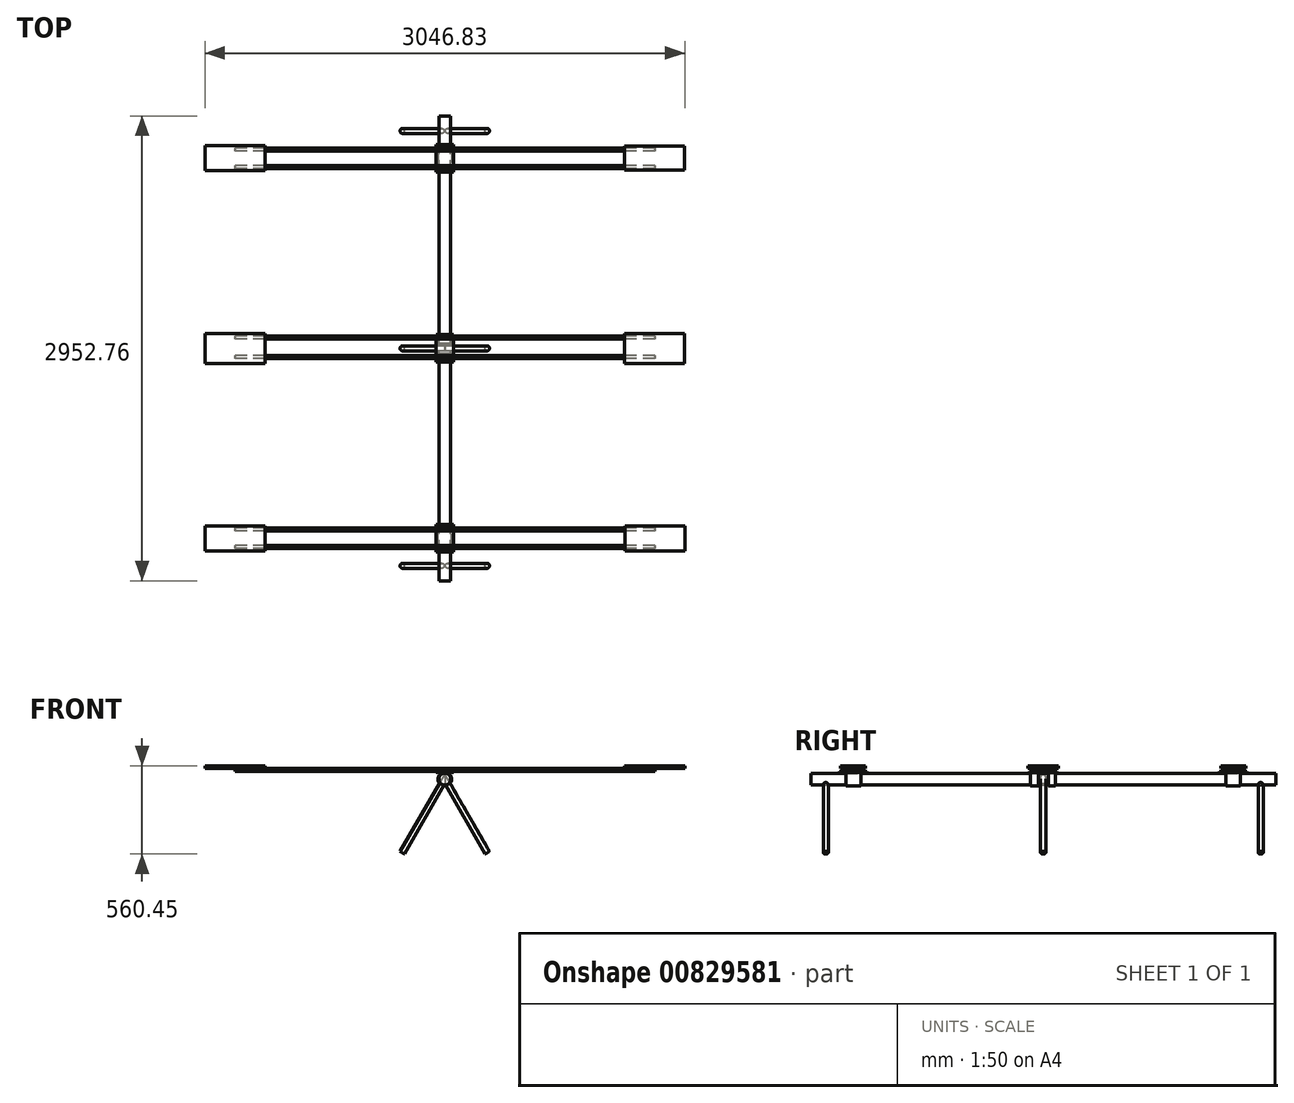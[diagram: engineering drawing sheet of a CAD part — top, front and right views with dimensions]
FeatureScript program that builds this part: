
annotation { "Feature Type Name" : "Feature", "Feature Type Description" : "" }
export const myFeature = defineFeature(function(context is Context, id is Id, definition is map)
    precondition{}
    {
        {
            var Q0;
            Q0=qCreatedBy(makeId("Right.planeOp"),FACE);
            var sketch = newSketch(context, id + "F0", { "sketchPlane" : qUnion([Q0])});
            skLineSegment(sketch, "E0", {"start": v(0, 0) * mm, "end": v(-1104.9, 0) * mm});
            skLineSegment(sketch, "E1", {"start": v(0, 0) * mm, "end": v(1104.9, 0) * mm});
            skPoint(sketch, "E2", {"position": v(-1104.9, 0) * mm});
            skPoint(sketch, "E3", {"position": v(1104.9, 0) * mm});
            skPoint(sketch, "E4", {"position": v(0, 0) * mm});
            skSolve(sketch);
        }
        {
            var Q0;
            Q0=sQuery(id+"F0.wireOp",VERTEX,"E2");
            var Q1;
            Q1=sQuery(id+"F0.wireOp",EDGE,"E0");
            cPlane(context, id + "F1", {"entities" : qUnion([Q0, Q1]), "cplaneType" : CPlaneType.LINE_POINT, "offset" : 25.4 * mm, "width" : 152.4 * mm, "height" : 152.4 * mm});
        }
        {
            var Q0;
            Q0=qCreatedBy(id+"F1.planeOp",FACE);
            var sketch = newSketch(context, id + "F2", { "sketchPlane" : qUnion([Q0])});
            skLineSegment(sketch, "E5", {"start": v(0, 0) * mm, "end": v(215.9, -373.95) * mm});
            skLineSegment(sketch, "E6", {"start": v(0, 0) * mm, "end": v(-215.9, -373.95) * mm});
            skSolve(sketch);
        }
        {
            var Q0;
            Q0=sQuery(id+"F0.wireOp",VERTEX,"E3");
            var Q1;
            Q1=sQuery(id+"F0.wireOp",EDGE,"E1");
            cPlane(context, id + "F3", {"entities" : qUnion([Q0, Q1]), "cplaneType" : CPlaneType.LINE_POINT, "offset" : 25.4 * mm, "width" : 152.4 * mm, "height" : 152.4 * mm});
        }
        {
            var Q0;
            Q0=qCreatedBy(id+"F3.planeOp",FACE);
            var sketch = newSketch(context, id + "F4", { "sketchPlane" : qUnion([Q0])});
            skLineSegment(sketch, "E7", {"start": v(0, 0) * mm, "end": v(215.9, -373.95) * mm});
            skLineSegment(sketch, "E8", {"start": v(0, 0) * mm, "end": v(-215.9, -373.95) * mm});
            skSolve(sketch);
        }
        {
            var Q0;
            Q0=qCreatedBy(makeId("Front.planeOp"),FACE);
            var sketch = newSketch(context, id + "F5", { "sketchPlane" : qUnion([Q0])});
            skLineSegment(sketch, "E9", {"start": v(0, 0) * mm, "end": v(215.9, -373.95) * mm});
            skLineSegment(sketch, "E10", {"start": v(0, 0) * mm, "end": v(-215.9, -373.95) * mm});
            skSolve(sketch);
        }
        {
            var Q0;
            Q0=qCreatedBy(id+"F1.planeOp",FACE);
            var sketch = newSketch(context, id + "F6", { "sketchPlane" : qUnion([Q0])});
            skCircle(sketch, "E11", {"center": v(0, 0) * mm, "radius": 30.16 * mm});
            skSolve(sketch);
        }
        {
            var Q0;
            Q0=makeQuery(id+"F6.imprint","IMPRINT",FACE,{"disambiguationData":[TD([[makeQuery(id+"F6.imprint","IMPRINT",EDGE,{"derivedFrom":sQuery(id+"F6.wireOp",EDGE,"E11")}),1.0]])]});
            var Q1;
            Q1=sQuery(id+"F6.wireOp",EDGE,"E11");
            var Q2;
            Q2=sQuery(id+"F0.wireOp",EDGE,"E0");
            var Q3;
            Q3=sQuery(id+"F0.wireOp",EDGE,"E1");
            sweep(context, id + "F7", {"profiles" : qUnion([Q0]), "surfaceProfiles" : qUnion([Q1]), "path" : qUnion([Q2, Q3])});
        }
        {
            var Q0;
            Q0=makeQuery(id+"F6.imprint","IMPRINT",FACE,{"disambiguationData":[TD([[makeQuery(id+"F6.imprint","IMPRINT",EDGE,{"derivedFrom":sQuery(id+"F6.wireOp",EDGE,"E11")}),1.0]])]});
            extrude(context, id + "F8", {"entities" : qUnion([Q0]), "operationType" : NewBodyOperationType.ADD, "depth" : 76.2 * mm, "offsetDistance" : 25.4 * mm});
        }
        {
            var Q0;
            Q0=sQuery(id+"F2.wireOp",EDGE,"E5");
            var Q1;
            Q1=sQuery(id+"F2.wireOp",VERTEX,"E5.end");
            cPlane(context, id + "F9", {"entities" : qUnion([Q0, Q1]), "cplaneType" : CPlaneType.LINE_POINT, "offset" : 25.4 * mm, "width" : 152.4 * mm, "height" : 152.4 * mm});
        }
        {
            var Q0;
            Q0=qCreatedBy(id+"F9.planeOp",FACE);
            var sketch = newSketch(context, id + "F10", { "sketchPlane" : qUnion([Q0])});
            skPoint(sketch, "E12", {"position": v(0, 1104.9) * mm});
            skCircle(sketch, "E13", {"center": v(0, 1104.9) * mm, "radius": 12.7 * mm});
            skSolve(sketch);
        }
        {
            var Q0;
            Q0=makeQuery(id+"F10.imprint","IMPRINT",FACE,{"disambiguationData":[TD([[makeQuery(id+"F10.imprint","IMPRINT",EDGE,{"derivedFrom":sQuery(id+"F10.wireOp",EDGE,"E13")}),1.0]])]});
            var Q1;
            Q1=sQuery(id+"F2.wireOp",EDGE,"E5");
            var Q2;
            Q2=sQuery(id+"F2.wireOp",EDGE,"E6");
            var Q3;
            Q3 = qConstructionFilter(qBodyType(qCreatedBy(id + "FF3xF3cxVK8Cgxf_1" ,EDGE), BodyType.WIRE), ConstructionObject.NO);
            sweep(context, id + "F11", {"operationType" : NewBodyOperationType.ADD, "profiles" : qUnion([Q0]), "path" : qUnion([Q1, Q2, Q3])});
        }
        {
            var Q0;
            Q0=qCreatedBy(id+"F9.planeOp",FACE);
            var sketch = newSketch(context, id + "F12", { "sketchPlane" : qUnion([Q0])});
            skCircle(sketch, "E14", {"center": v(0, 0) * mm, "radius": 12.7 * mm});
            skSolve(sketch);
        }
        {
            var Q0;
            Q0=makeQuery(id+"F12.imprint","IMPRINT",FACE,{"disambiguationData":[TD([[makeQuery(id+"F12.imprint","IMPRINT",EDGE,{"derivedFrom":sQuery(id+"F12.wireOp",EDGE,"E14")}),1.0]])]});
            var Q1;
            Q1=sQuery(id+"F12.wireOp",EDGE,"E14");
            var Q2;
            Q2=sQuery(id+"F5.wireOp",EDGE,"E9");
            var Q3;
            Q3=sQuery(id+"F5.wireOp",EDGE,"E10");
            sweep(context, id + "F13", {"profiles" : qUnion([Q0]), "surfaceProfiles" : qUnion([Q1]), "path" : qUnion([Q2, Q3])});
        }
        {
            var Q0;
            Q0=qCreatedBy(id+"F9.planeOp",FACE);
            var sketch = newSketch(context, id + "F14", { "sketchPlane" : qUnion([Q0])});
            skCircle(sketch, "E15", {"center": v(0, -1104.9) * mm, "radius": 12.7 * mm});
            skSolve(sketch);
        }
        {
            var Q0;
            Q0=makeQuery(id+"F14.imprint","IMPRINT",FACE,{"disambiguationData":[TD([[makeQuery(id+"F14.imprint","IMPRINT",EDGE,{"derivedFrom":sQuery(id+"F14.wireOp",EDGE,"E15")}),1.0]])]});
            var Q1;
            Q1=sQuery(id+"F4.wireOp",EDGE,"E8");
            var Q2;
            Q2=sQuery(id+"F4.wireOp",EDGE,"E7");
            sweep(context, id + "F15", {"operationType" : NewBodyOperationType.ADD, "profiles" : qUnion([Q0]), "path" : qUnion([Q1, Q2])});
        }
        {
            var Q0;
            Q0=sQuery(id+"F4.wireOp",VERTEX,"E7.start");
            var Q1;
            {var subQ0=sQuery(id+"F6.wireOp",EDGE,"E11");Q1=makeQuery(id+"F8.boolean.opBoolean","MERGE",FACE,{"derivedFrom":[makeQuery(id+"F7.opSweep","SWEPT_FACE",FACE,{"disambiguationData":[OSD([sQuery(id+"F0.wireOp",EDGE,"E0"),subQ0])]}),makeQuery(id+"F8.opExtrude","SWEPT_FACE",FACE,{"disambiguationData":[OSD([subQ0])]})]});}
            cPlane(context, id + "F16", {"entities" : qUnion([Q0, Q1]), "cplaneType" : CPlaneType.LINE_POINT, "offset" : 25.4 * mm, "width" : 152.4 * mm, "height" : 152.4 * mm});
        }
        {
            var Q0;
            Q0=qCreatedBy(id+"F16.planeOp",FACE);
            var sketch = newSketch(context, id + "F17", { "sketchPlane" : qUnion([Q0])});
            skPoint(sketch, "E16", {"position": v(0, 0) * mm});
            skCircle(sketch, "E17", {"center": v(0, 0) * mm, "radius": 30.16 * mm});
            skSolve(sketch);
        }
        {
            var Q0;
            Q0 = qSketchRegion(id + "F17", true);
            extrude(context, id + "F18", {"entities" : qUnion([Q0]), "operationType" : NewBodyOperationType.ADD, "depth" : 76.2 * mm, "offsetDistance" : 25.4 * mm});
        }
        {
            var Q0;
            Q0=qCreatedBy(makeId("Right.planeOp"),FACE);
            var sketch = newSketch(context, id + "F19", { "sketchPlane" : qUnion([Q0])});
            skLineSegment(sketch, "E18", {"start": v(0, 0) * mm, "end": v(-965.2, 0) * mm});
            skLineSegment(sketch, "E19", {"start": v(0, 0) * mm, "end": v(965.2, 0) * mm});
            skSolve(sketch);
        }
        {
            var Q0;
            Q0=sQuery(id+"F19.wireOp",VERTEX,"E18.end");
            var Q1;
            Q1=sQuery(id+"F19.wireOp",EDGE,"E18");
            cPlane(context, id + "F20", {"entities" : qUnion([Q0, Q1]), "cplaneType" : CPlaneType.LINE_POINT, "offset" : 25.4 * mm, "width" : 152.4 * mm, "height" : 152.4 * mm});
        }
        {
            var Q0;
            Q0=qCreatedBy(id+"F20.planeOp",FACE);
            var sketch = newSketch(context, id + "F21", { "sketchPlane" : qUnion([Q0])});
            skPoint(sketch, "E20", {"position": v(0, 0) * mm});
            skCircle(sketch, "E21", {"center": v(0, 0) * mm, "radius": 34.93 * mm});
            skSolve(sketch);
        }
        {
            var Q0;
            Q0=makeQuery(id+"F21.imprint","IMPRINT",FACE,{"disambiguationData":[TD([[makeQuery(id+"F21.imprint","IMPRINT",EDGE,{"derivedFrom":sQuery(id+"F21.wireOp",EDGE,"E21")}),1.0]])]});
            extrude(context, id + "F22", {"entities" : qUnion([Q0]), "depth" : 38.1 * mm, "offsetDistance" : 25.4 * mm, "hasSecondDirection" : true, "secondDirectionOppositeDirection" : true, "secondDirectionDepth" : 38.1 * mm});
        }
        {
            var Q0;
            Q0=sQuery(id+"F19.wireOp",VERTEX,"E19.end");
            var Q1;
            Q1=sQuery(id+"F19.wireOp",EDGE,"E19");
            cPlane(context, id + "F23", {"entities" : qUnion([Q0, Q1]), "cplaneType" : CPlaneType.LINE_POINT, "offset" : 25.4 * mm, "width" : 152.4 * mm, "height" : 152.4 * mm});
        }
        {
            var Q0;
            Q0=qCreatedBy(id+"F23.planeOp",FACE);
            var sketch = newSketch(context, id + "F24", { "sketchPlane" : qUnion([Q0])});
            skPoint(sketch, "E22", {"position": v(0, 0) * mm});
            skCircle(sketch, "E23", {"center": v(0, 0) * mm, "radius": 34.93 * mm});
            skSolve(sketch);
        }
        {
            var Q0;
            Q0 = qSketchRegion(id + "F24", true);
            extrude(context, id + "F25", {"entities" : qUnion([Q0]), "depth" : 38.1 * mm, "offsetDistance" : 25.4 * mm, "hasSecondDirection" : true, "secondDirectionOppositeDirection" : true, "secondDirectionDepth" : 38.1 * mm});
        }
        {
            var Q0;
            Q0=qCreatedBy(makeId("Right.planeOp"),FACE);
            var sketch = newSketch(context, id + "F26", { "sketchPlane" : qUnion([Q0])});
            skLineSegment(sketch, "E24", {"start": v(0, 0) * mm, "end": v(-25.4, 0) * mm});
            skLineSegment(sketch, "E25", {"start": v(0, 0) * mm, "end": v(25.4, 0) * mm});
            skSolve(sketch);
        }
        {
            var Q0;
            Q0=sQuery(id+"F26.wireOp",VERTEX,"E24.end");
            var Q1;
            Q1=sQuery(id+"F26.wireOp",EDGE,"E24");
            cPlane(context, id + "F27", {"entities" : qUnion([Q0, Q1]), "cplaneType" : CPlaneType.LINE_POINT, "offset" : 25.4 * mm, "width" : 152.4 * mm, "height" : 152.4 * mm});
        }
        {
            var Q0;
            Q0=qCreatedBy(id+"F27.planeOp",FACE);
            var sketch = newSketch(context, id + "F28", { "sketchPlane" : qUnion([Q0])});
            skPoint(sketch, "E26", {"position": v(0, 0) * mm});
            skCircle(sketch, "E27", {"center": v(0, 0) * mm, "radius": 34.93 * mm});
            skSolve(sketch);
        }
        {
            var Q0;
            Q0 = qSketchRegion(id + "F28", true);
            extrude(context, id + "F29", {"entities" : qUnion([Q0]), "depth" : 38.1 * mm, "offsetDistance" : 25.4 * mm});
        }
        {
            var Q0;
            Q0=sQuery(id+"F26.wireOp",VERTEX,"E25.end");
            var Q1;
            Q1=sQuery(id+"F26.wireOp",EDGE,"E25");
            cPlane(context, id + "F30", {"entities" : qUnion([Q0, Q1]), "cplaneType" : CPlaneType.LINE_POINT, "offset" : 25.4 * mm, "width" : 152.4 * mm, "height" : 152.4 * mm});
        }
        {
            var Q0;
            Q0=qCreatedBy(id+"F30.planeOp",FACE);
            var sketch = newSketch(context, id + "F31", { "sketchPlane" : qUnion([Q0])});
            skCircle(sketch, "E28", {"center": v(0, 0) * mm, "radius": 34.93 * mm});
            skSolve(sketch);
        }
        {
            var Q0;
            Q0 = qSketchRegion(id + "F31", true);
            extrude(context, id + "F32", {"entities" : qUnion([Q0]), "depth" : 38.1 * mm, "offsetDistance" : 25.4 * mm});
        }
        {
            var Q0;
            Q0=qCreatedBy(id+"F27.planeOp",FACE);
            var sketch = newSketch(context, id + "F33", { "sketchPlane" : qUnion([Q0])});
            skLineSegment(sketch, "E29", {"start": v(0, 0) * mm, "end": v(0, 34.93) * mm});
            skSolve(sketch);
        }
        {
            var Q0;
            Q0=sQuery(id+"F33.wireOp",EDGE,"E29");
            var Q1;
            Q1=sQuery(id+"F33.wireOp",VERTEX,"E29.end");
            cPlane(context, id + "F34", {"entities" : qUnion([Q0, Q1]), "cplaneType" : CPlaneType.LINE_POINT, "offset" : 25.4 * mm, "width" : 152.4 * mm, "height" : 152.4 * mm});
        }
        {
            var Q0;
            Q0=qCreatedBy(id+"F34.planeOp",FACE);
            var sketch = newSketch(context, id + "F35", { "sketchPlane" : qUnion([Q0])});
            skLineSegment(sketch, "E30.bottom", {"start": v(44.45, -69.85) * mm, "end": v(-44.45, -69.85) * mm});
            skLineSegment(sketch, "E30.top", {"start": v(44.45, 69.85) * mm, "end": v(-44.45, 69.85) * mm});
            skLineSegment(sketch, "E30.left", {"start": v(44.45, -69.85) * mm, "end": v(44.45, 69.85) * mm});
            skLineSegment(sketch, "E30.right", {"start": v(-44.45, -69.85) * mm, "end": v(-44.45, 69.85) * mm});
            skPoint(sketch, "E30.middle", {"position": v(0, 0) * mm});
            skSolve(sketch);
        }
        {
            var Q0;
            Q0=qCreatedBy(id+"F34.planeOp",FACE);
            var sketch = newSketch(context, id + "F36", { "sketchPlane" : qUnion([Q0])});
            skLineSegment(sketch, "E31.bottom", {"start": v(44.45, -1034.7) * mm, "end": v(-44.45, -1034.7) * mm});
            skLineSegment(sketch, "E31.top", {"start": v(44.45, -895) * mm, "end": v(-44.45, -895) * mm});
            skLineSegment(sketch, "E31.left", {"start": v(44.45, -1034.7) * mm, "end": v(44.45, -895) * mm});
            skLineSegment(sketch, "E31.right", {"start": v(-44.45, -1034.7) * mm, "end": v(-44.45, -895) * mm});
            skPoint(sketch, "E31.middle", {"position": v(0, -964.86) * mm});
            skSolve(sketch);
        }
        {
            var Q0;
            Q0=qCreatedBy(id+"F34.planeOp",FACE);
            var sketch = newSketch(context, id + "F37", { "sketchPlane" : qUnion([Q0])});
            skLineSegment(sketch, "E32.bottom", {"start": v(44.45, 895.7) * mm, "end": v(-44.45, 895.7) * mm});
            skLineSegment(sketch, "E32.top", {"start": v(44.45, 1035.4) * mm, "end": v(-44.45, 1035.4) * mm});
            skLineSegment(sketch, "E32.left", {"start": v(44.45, 895.7) * mm, "end": v(44.45, 1035.4) * mm});
            skLineSegment(sketch, "E32.right", {"start": v(-44.45, 895.7) * mm, "end": v(-44.45, 1035.4) * mm});
            skPoint(sketch, "E32.middle", {"position": v(0, 965.55) * mm});
            skSolve(sketch);
        }
        {
            var Q0;
            Q0 = qSketchRegion(id + "F37", true);
            extrude(context, id + "F38", {"entities" : qUnion([Q0]), "operationType" : NewBodyOperationType.ADD, "depth" : 5.08 * mm, "offsetDistance" : 25.4 * mm});
        }
        {
            var Q0;
            Q0 = qSketchRegion(id + "F36", true);
            extrude(context, id + "F39", {"entities" : qUnion([Q0]), "operationType" : NewBodyOperationType.ADD, "depth" : 5.08 * mm, "offsetDistance" : 25.4 * mm});
        }
        {
            var Q0;
            Q0 = qSketchRegion(id + "F35", true);
            extrude(context, id + "F40", {"entities" : qUnion([Q0]), "depth" : 5.08 * mm, "offsetDistance" : 25.4 * mm});
        }
        {
            var Q0;
            Q0=makeQuery(id+"F39.opExtrude","CAP_EDGE",EDGE,{"disambiguationData":[OSD([sQuery(id+"F36.wireOp",EDGE,"E31.left")])],"isStart":true});
            cPoint(context, id + "F41", {"entities" : qUnion([Q0]), "parameter" : 0.5});
        }
        {
            var Q0;
            Q0 = qCreatedBy(id + "F41" ,VERTEX);
            var Q1;
            Q1=makeQuery(id+"F39.opExtrude","CAP_EDGE",EDGE,{"disambiguationData":[OSD([sQuery(id+"F36.wireOp",EDGE,"E31.left")])],"isStart":false});
            cPlane(context, id + "F42", {"entities" : qUnion([Q0, Q1]), "cplaneType" : CPlaneType.LINE_POINT, "offset" : 25.4 * mm, "width" : 152.4 * mm, "height" : 152.4 * mm});
        }
        {
            var Q0;
            Q0=qCreatedBy(id+"F42.planeOp",FACE);
            var sketch = newSketch(context, id + "F43", { "sketchPlane" : qUnion([Q0])});
            skLineSegment(sketch, "E33", {"start": v(0, 34.93) * mm, "end": v(0, 47.63) * mm});
            skSolve(sketch);
        }
        {
            var Q0;
            Q0=sQuery(id+"F43.wireOp",EDGE,"E33");
            var Q1;
            Q1=sQuery(id+"F43.wireOp",VERTEX,"E33.end");
            cPlane(context, id + "F44", {"entities" : qUnion([Q0, Q1]), "cplaneType" : CPlaneType.LINE_POINT, "offset" : 25.4 * mm, "width" : 152.4 * mm, "height" : 152.4 * mm});
        }
        {
            var Q0;
            Q0=qCreatedBy(id+"F44.planeOp",FACE);
            var sketch = newSketch(context, id + "F45", { "sketchPlane" : qUnion([Q0])});
            skLineSegment(sketch, "E34", {"start": v(0, -1034.04) * mm, "end": v(0, -1008.64) * mm});
            skLineSegment(sketch, "E35", {"start": v(0, -894.41) * mm, "end": v(0, -919.81) * mm});
            skLineSegment(sketch, "E36", {"start": v(0, -919.81) * mm, "end": v(-1066.8, -919.81) * mm});
            skLineSegment(sketch, "E37", {"start": v(0, -919.81) * mm, "end": v(1066.8, -919.81) * mm});
            skLineSegment(sketch, "E38", {"start": v(0, -1008.64) * mm, "end": v(1066.8, -1008.64) * mm});
            skLineSegment(sketch, "E39", {"start": v(0, -1008.64) * mm, "end": v(-1066.8, -1008.64) * mm});
            skPoint(sketch, "E40", {"position": v(1066.8, -919.81) * mm});
            skSolve(sketch);
        }
        {
            var Q0;
            Q0=sQuery(id+"F45.wireOp",EDGE,"E37");
            var Q1;
            Q1=sQuery(id+"F45.wireOp",VERTEX,"E37.end");
            cPlane(context, id + "F46", {"entities" : qUnion([Q0, Q1]), "cplaneType" : CPlaneType.LINE_POINT, "offset" : 25.4 * mm, "width" : 152.4 * mm, "height" : 152.4 * mm});
        }
        {
            var Q0;
            Q0=qCreatedBy(id+"F46.planeOp",FACE);
            var sketch = newSketch(context, id + "F47", { "sketchPlane" : qUnion([Q0])});
            skPoint(sketch, "E41", {"position": v(-1008.64, 47.64) * mm});
            skCircle(sketch, "E42", {"center": v(-1008.64, 47.64) * mm, "radius": 7.62 * mm});
            skSolve(sketch);
        }
        {
            var Q0;
            Q0=makeQuery(id+"F47.imprint","IMPRINT",FACE,{"disambiguationData":[TD([[makeQuery(id+"F47.imprint","IMPRINT",EDGE,{"derivedFrom":sQuery(id+"F47.wireOp",EDGE,"E42")}),1.0]])]});
            var Q1;
            Q1 = qSketchRegion(id + "F45", true);
            var Q2;
            Q2=sQuery(id+"F47.wireOp",EDGE,"E42");
            var Q3;
            Q3=sQuery(id+"F45.wireOp",EDGE,"E38");
            var Q4;
            Q4=sQuery(id+"F45.wireOp",EDGE,"E39");
            sweep(context, id + "F48", {"profiles" : qUnion([Q0, Q1]), "surfaceProfiles" : qUnion([Q2]), "path" : qUnion([Q3, Q4])});
        }
        {
            var Q0;
            Q0=qCreatedBy(id+"F46.planeOp",FACE);
            var sketch = newSketch(context, id + "F49", { "sketchPlane" : qUnion([Q0])});
            skCircle(sketch, "E43", {"center": v(-919.81, 47.63) * mm, "radius": 7.62 * mm});
            skSolve(sketch);
        }
        {
            var Q0;
            Q0=makeQuery(id+"F49.imprint","IMPRINT",FACE,{"disambiguationData":[TD([[makeQuery(id+"F49.imprint","IMPRINT",EDGE,{"derivedFrom":sQuery(id+"F49.wireOp",EDGE,"E43")}),1.0]])]});
            var Q1;
            Q1=sQuery(id+"F49.wireOp",EDGE,"E43");
            var Q2;
            Q2=sQuery(id+"F45.wireOp",EDGE,"E37");
            var Q3;
            Q3=sQuery(id+"F45.wireOp",EDGE,"E36");
            sweep(context, id + "F50", {"profiles" : qUnion([Q0]), "surfaceProfiles" : qUnion([Q1]), "path" : qUnion([Q2, Q3])});
        }
        {
            var Q0;
            Q0=qCreatedBy(id+"F44.planeOp",FACE);
            var sketch = newSketch(context, id + "F51", { "sketchPlane" : qUnion([Q0])});
            skLineSegment(sketch, "E44", {"start": v(0, -69.3) * mm, "end": v(0, -43.9) * mm});
            skLineSegment(sketch, "E45", {"start": v(0, 69.92) * mm, "end": v(0, 55.3) * mm});
            skLineSegment(sketch, "E46", {"start": v(0, -43.9) * mm, "end": v(1066.8, -43.9) * mm});
            skLineSegment(sketch, "E47", {"start": v(0, 55.3) * mm, "end": v(1066.8, 55.3) * mm});
            skLineSegment(sketch, "E48", {"start": v(0, 55.3) * mm, "end": v(-1066.8, 55.3) * mm});
            skLineSegment(sketch, "E49", {"start": v(0, -43.9) * mm, "end": v(-1066.8, -43.9) * mm});
            skSolve(sketch);
        }
        {
            var Q0;
            Q0=qCreatedBy(id+"F46.planeOp",FACE);
            var sketch = newSketch(context, id + "F52", { "sketchPlane" : qUnion([Q0])});
            skPoint(sketch, "E50", {"position": v(-43.9, 47.63) * mm});
            skCircle(sketch, "E51", {"center": v(-43.9, 47.63) * mm, "radius": 7.62 * mm});
            skPoint(sketch, "E52", {"position": v(55.3, 47.63) * mm});
            skCircle(sketch, "E53", {"center": v(55.3, 47.63) * mm, "radius": 7.62 * mm});
            skSolve(sketch);
        }
        {
            var Q0;
            Q0=makeQuery(id+"F52.imprint","IMPRINT",FACE,{"disambiguationData":[TD([[makeQuery(id+"F52.imprint","IMPRINT",EDGE,{"derivedFrom":sQuery(id+"F52.wireOp",EDGE,"E51")}),1.0]])]});
            var Q1;
            Q1=sQuery(id+"F52.wireOp",EDGE,"E51");
            var Q2;
            Q2=sQuery(id+"F51.wireOp",EDGE,"E46");
            var Q3;
            Q3=sQuery(id+"F51.wireOp",EDGE,"E49");
            sweep(context, id + "F53", {"profiles" : qUnion([Q0]), "surfaceProfiles" : qUnion([Q1]), "path" : qUnion([Q2, Q3])});
        }
        {
            var Q0;
            Q0=makeQuery(id+"F52.imprint","IMPRINT",FACE,{"disambiguationData":[TD([[makeQuery(id+"F52.imprint","IMPRINT",EDGE,{"derivedFrom":sQuery(id+"F52.wireOp",EDGE,"E53")}),1.0]])]});
            var Q1;
            Q1=sQuery(id+"F51.wireOp",EDGE,"E47");
            var Q2;
            Q2=sQuery(id+"F51.wireOp",EDGE,"E48");
            sweep(context, id + "F54", {"profiles" : qUnion([Q0]), "path" : qUnion([Q1, Q2])});
        }
        {
            var Q0;
            Q0=qCreatedBy(id+"F44.planeOp",FACE);
            var sketch = newSketch(context, id + "F55", { "sketchPlane" : qUnion([Q0])});
            skLineSegment(sketch, "E54", {"start": v(0, 895.8) * mm, "end": v(0, 921.2) * mm});
            skLineSegment(sketch, "E55", {"start": v(0, 1035.4) * mm, "end": v(0, 1010) * mm});
            skLineSegment(sketch, "E56", {"start": v(0, 921.2) * mm, "end": v(1066.8, 921.2) * mm});
            skLineSegment(sketch, "E57", {"start": v(0, 921.2) * mm, "end": v(-1066.8, 921.2) * mm});
            skLineSegment(sketch, "E58", {"start": v(0, 1010) * mm, "end": v(1066.8, 1010) * mm});
            skLineSegment(sketch, "E59", {"start": v(0, 1010) * mm, "end": v(-1066.8, 1010) * mm});
            skSolve(sketch);
        }
        {
            var Q0;
            Q0=qCreatedBy(id+"F46.planeOp",FACE);
            var sketch = newSketch(context, id + "F56", { "sketchPlane" : qUnion([Q0])});
            skPoint(sketch, "E60", {"position": v(921.2, 47.63) * mm});
            skCircle(sketch, "E61", {"center": v(921.2, 47.63) * mm, "radius": 7.62 * mm});
            skPoint(sketch, "E62", {"position": v(1010, 47.63) * mm});
            skCircle(sketch, "E63", {"center": v(1010, 47.63) * mm, "radius": 7.62 * mm});
            skSolve(sketch);
        }
        {
            var Q0;
            Q0=makeQuery(id+"F56.imprint","IMPRINT",FACE,{"disambiguationData":[TD([[makeQuery(id+"F56.imprint","IMPRINT",EDGE,{"derivedFrom":sQuery(id+"F56.wireOp",EDGE,"E61")}),1.0]])]});
            var Q1;
            Q1=sQuery(id+"F55.wireOp",EDGE,"E56");
            var Q2;
            Q2=sQuery(id+"F55.wireOp",EDGE,"E57");
            sweep(context, id + "F57", {"profiles" : qUnion([Q0]), "path" : qUnion([Q1, Q2])});
        }
        {
            var Q0;
            Q0=makeQuery(id+"F56.imprint","IMPRINT",FACE,{"disambiguationData":[TD([[makeQuery(id+"F56.imprint","IMPRINT",EDGE,{"derivedFrom":sQuery(id+"F56.wireOp",EDGE,"E63")}),1.0]])]});
            var Q1;
            Q1=sQuery(id+"F56.wireOp",EDGE,"E63");
            var Q2;
            Q2=sQuery(id+"F55.wireOp",EDGE,"E58");
            var Q3;
            Q3=sQuery(id+"F55.wireOp",EDGE,"E59");
            sweep(context, id + "F58", {"profiles" : qUnion([Q0]), "surfaceProfiles" : qUnion([Q1]), "path" : qUnion([Q2, Q3])});
        }
        {
            var Q0;
            Q0=qCreatedBy(id+"F46.planeOp",FACE);
            var sketch = newSketch(context, id + "F59", { "sketchPlane" : qUnion([Q0])});
            skLineSegment(sketch, "E64", {"start": v(-964.86, 47.74) * mm, "end": v(-964.86, 55.36) * mm});
            skSolve(sketch);
        }
        {
            var Q0;
            Q0=sQuery(id+"F59.wireOp",EDGE,"E64");
            var Q1;
            Q1=sQuery(id+"F59.wireOp",VERTEX,"E64.end");
            cPlane(context, id + "F60", {"entities" : qUnion([Q0, Q1]), "cplaneType" : CPlaneType.LINE_POINT, "offset" : 25.4 * mm, "width" : 152.4 * mm, "height" : 152.4 * mm});
        }
        {
            var Q0;
            Q0=qCreatedBy(id+"F60.planeOp",FACE);
            var sketch = newSketch(context, id + "F61", { "sketchPlane" : qUnion([Q0])});
            skPoint(sketch, "E65", {"position": v(1066.85, -965.49) * mm});
            skLineSegment(sketch, "E66.bottom", {"start": v(1219.25, -1028.99) * mm, "end": v(914.45, -1028.99) * mm});
            skLineSegment(sketch, "E66.top", {"start": v(1219.25, -901.99) * mm, "end": v(914.45, -901.99) * mm});
            skLineSegment(sketch, "E66.left", {"start": v(1219.25, -1028.99) * mm, "end": v(1219.25, -901.99) * mm});
            skLineSegment(sketch, "E66.right", {"start": v(914.45, -1028.99) * mm, "end": v(914.45, -901.99) * mm});
            skLineSegment(sketch, "E67.bottom", {"start": v(1219.07, 905.67) * mm, "end": v(914.27, 905.67) * mm});
            skLineSegment(sketch, "E67.top", {"start": v(1219.07, 1027.1) * mm, "end": v(914.27, 1027.1) * mm});
            skLineSegment(sketch, "E67.left", {"start": v(1219.07, 905.67) * mm, "end": v(1219.07, 1027.1) * mm});
            skLineSegment(sketch, "E67.right", {"start": v(914.27, 905.67) * mm, "end": v(914.27, 1027.1) * mm});
            skPoint(sketch, "E67.middle", {"position": v(1066.67, 966.38) * mm});
            skLineSegment(sketch, "E68.bottom", {"start": v(1218.5, -76.2) * mm, "end": v(913.7, -76.2) * mm});
            skLineSegment(sketch, "E68.top", {"start": v(1218.5, 76.2) * mm, "end": v(913.7, 76.2) * mm});
            skLineSegment(sketch, "E68.left", {"start": v(1218.5, -76.2) * mm, "end": v(1218.5, 76.2) * mm});
            skLineSegment(sketch, "E68.right", {"start": v(913.7, -76.2) * mm, "end": v(913.7, 76.2) * mm});
            skPoint(sketch, "E68.middle", {"position": v(1066.1, 0) * mm});
            skLineSegment(sketch, "E69", {"start": v(1066.67, 966.38) * mm, "end": v(-1065.82, 966.38) * mm});
            skLineSegment(sketch, "E70", {"start": v(-1065.82, 966.38) * mm, "end": v(-1065.82, -1019.27) * mm});
            skLineSegment(sketch, "E71", {"start": v(1066.1, 0) * mm, "end": v(-1065.82, 0) * mm});
            skLineSegment(sketch, "E72", {"start": v(1066.85, -965.49) * mm, "end": v(-1065.82, -965.49) * mm});
            skLineSegment(sketch, "E73.bottom", {"start": v(-913.42, 902.88) * mm, "end": v(-1218.22, 902.88) * mm});
            skLineSegment(sketch, "E73.top", {"start": v(-913.42, 1029.88) * mm, "end": v(-1218.22, 1029.88) * mm});
            skLineSegment(sketch, "E73.left", {"start": v(-913.42, 902.88) * mm, "end": v(-913.42, 1029.88) * mm});
            skLineSegment(sketch, "E73.right", {"start": v(-1218.22, 902.88) * mm, "end": v(-1218.22, 1029.88) * mm});
            skPoint(sketch, "E73.middle", {"position": v(-1065.82, 966.38) * mm});
            skLineSegment(sketch, "E74.bottom", {"start": v(-913.42, -76.2) * mm, "end": v(-1218.22, -76.2) * mm});
            skLineSegment(sketch, "E74.top", {"start": v(-913.42, 76.2) * mm, "end": v(-1218.22, 76.2) * mm});
            skLineSegment(sketch, "E74.left", {"start": v(-913.42, -76.2) * mm, "end": v(-913.42, 76.2) * mm});
            skLineSegment(sketch, "E74.right", {"start": v(-1218.22, -76.2) * mm, "end": v(-1218.22, 76.2) * mm});
            skPoint(sketch, "E74.middle", {"position": v(-1065.82, 0) * mm});
            skLineSegment(sketch, "E75.bottom", {"start": v(-913.42, -1028.99) * mm, "end": v(-1218.22, -1028.99) * mm});
            skLineSegment(sketch, "E75.top", {"start": v(-913.42, -901.99) * mm, "end": v(-1218.22, -901.99) * mm});
            skLineSegment(sketch, "E75.left", {"start": v(-913.42, -1028.99) * mm, "end": v(-913.42, -901.99) * mm});
            skLineSegment(sketch, "E75.right", {"start": v(-1218.22, -1028.99) * mm, "end": v(-1218.22, -901.99) * mm});
            skPoint(sketch, "E75.middle", {"position": v(-1065.82, -965.49) * mm});
            skSolve(sketch);
        }
        {
            var Q0;
            {var subQ4=sQuery(id+"F61.wireOp",EDGE,"E75.bottom");Q0=makeQuery(id+"F61.imprint","IMPRINT",FACE,{"disambiguationData":[TD([[makeQuery(id+"F61.imprint","IMPRINT",EDGE,{"derivedFrom":subQ4}),-1.0]])]});}
            var Q1;
            {var subQ0=sQuery(id+"F61.wireOp",EDGE,"E72");var subQ1=sQuery(id+"F61.wireOp",EDGE,"E70");var subQ2=makeQuery(id+"F61.imprint","INTERSECT",VERTEX,{"derivedFrom":[subQ1,subQ0]});Q1=makeQuery(id+"F61.imprint","IMPRINT",FACE,{"disambiguationData":[TD([[makeQuery(id+"F61.imprint","IMPRINT",EDGE,{"disambiguationData":[TD([[subQ2,1.0]])],"derivedFrom":subQ1}),1.0]])]});}
            extrude(context, id + "F62", {"entities" : qUnion([Q0, Q1]), "depth" : 12.7 * mm, "offsetDistance" : 25.4 * mm});
        }
        {
            var Q0;
            {var subQ0=sQuery(id+"F61.wireOp",EDGE,"E74.right");Q0=makeQuery(id+"F61.imprint","IMPRINT",FACE,{"disambiguationData":[TD([[makeQuery(id+"F61.imprint","IMPRINT",EDGE,{"derivedFrom":subQ0}),-1.0]])]});}
            var Q1;
            {var subQ0=sQuery(id+"F61.wireOp",EDGE,"E71");var subQ1=sQuery(id+"F61.wireOp",EDGE,"E70");var subQ2=makeQuery(id+"F61.imprint","INTERSECT",VERTEX,{"derivedFrom":[subQ1,subQ0]});Q1=makeQuery(id+"F61.imprint","IMPRINT",FACE,{"disambiguationData":[TD([[makeQuery(id+"F61.imprint","IMPRINT",EDGE,{"disambiguationData":[TD([[subQ2,1.0]])],"derivedFrom":subQ1}),1.0]])]});}
            var Q2;
            {var subQ0=sQuery(id+"F61.wireOp",EDGE,"E71");var subQ1=sQuery(id+"F61.wireOp",EDGE,"E70");var subQ2=makeQuery(id+"F61.imprint","INTERSECT",VERTEX,{"derivedFrom":[subQ1,subQ0]});Q2=makeQuery(id+"F61.imprint","IMPRINT",FACE,{"disambiguationData":[TD([[makeQuery(id+"F61.imprint","IMPRINT",EDGE,{"disambiguationData":[TD([[subQ2,-1.0]])],"derivedFrom":subQ1}),1.0]])]});}
            var Q3;
            {var subQ0=sQuery(id+"F61.wireOp",EDGE,"E73.top");Q3=makeQuery(id+"F61.imprint","IMPRINT",FACE,{"disambiguationData":[TD([[makeQuery(id+"F61.imprint","IMPRINT",EDGE,{"derivedFrom":subQ0}),1.0]])]});}
            var Q4;
            {var subQ0=sQuery(id+"F61.wireOp",EDGE,"E70");var subQ1=sQuery(id+"F61.wireOp",EDGE,"E69");var subQ2=makeQuery(id+"F61.imprint","INTERSECT",VERTEX,{"derivedFrom":[subQ1,subQ0]});Q4=makeQuery(id+"F61.imprint","IMPRINT",FACE,{"disambiguationData":[TD([[makeQuery(id+"F61.imprint","IMPRINT",EDGE,{"disambiguationData":[TD([[subQ2,1.0]])],"derivedFrom":subQ1}),1.0]])]});}
            var Q5;
            {var subQ1=sQuery(id+"F61.wireOp",EDGE,"E67.bottom");Q5=makeQuery(id+"F61.imprint","IMPRINT",FACE,{"disambiguationData":[TD([[makeQuery(id+"F61.imprint","IMPRINT",EDGE,{"derivedFrom":subQ1}),-1.0]])]});}
            var Q6;
            {var subQ1=sQuery(id+"F61.wireOp",EDGE,"E68.bottom");Q6=makeQuery(id+"F61.imprint","IMPRINT",FACE,{"disambiguationData":[TD([[makeQuery(id+"F61.imprint","IMPRINT",EDGE,{"derivedFrom":subQ1}),-1.0]])]});}
            var Q7;
            {var subQ1=sQuery(id+"F61.wireOp",EDGE,"E66.bottom");Q7=makeQuery(id+"F61.imprint","IMPRINT",FACE,{"disambiguationData":[TD([[makeQuery(id+"F61.imprint","IMPRINT",EDGE,{"derivedFrom":subQ1}),-1.0]])]});}
            extrude(context, id + "F63", {"entities" : qUnion([Q0, Q1, Q2, Q3, Q4, Q5, Q6, Q7]), "depth" : 12.7 * mm, "offsetDistance" : 25.4 * mm});
        }
        {
            var Q0;
            Q0=makeQuery(id+"F48.opSweep","SWEPT_BODY",BODY,{"disambiguationData":[OSD([sQuery(id+"F45.wireOp",EDGE,"E39"),sQuery(id+"F47.wireOp",EDGE,"E42")])]});
            var Q1;
            Q1=makeQuery(id+"F7.opSweep","SWEPT_BODY",BODY,{"disambiguationData":[OSD([sQuery(id+"F0.wireOp",EDGE,"E1"),sQuery(id+"F6.wireOp",EDGE,"E11")])]});
            var Q2;
            Q2=makeQuery(id+"F50.opSweep","SWEPT_BODY",BODY,{"disambiguationData":[OSD([sQuery(id+"F45.wireOp",EDGE,"E36"),sQuery(id+"F49.wireOp",EDGE,"E43")])]});
            var Q3;
            Q3=makeQuery(id+"F53.opSweep","SWEPT_BODY",BODY,{"disambiguationData":[OSD([sQuery(id+"F51.wireOp",EDGE,"E49"),sQuery(id+"F52.wireOp",EDGE,"E51")])]});
            var Q4;
            Q4=makeQuery(id+"F54.opSweep","SWEPT_BODY",BODY,{"disambiguationData":[OSD([sQuery(id+"F51.wireOp",EDGE,"E48"),sQuery(id+"F52.wireOp",EDGE,"E53")])]});
            var Q5;
            Q5=makeQuery(id+"F57.opSweep","SWEPT_BODY",BODY,{"disambiguationData":[OSD([sQuery(id+"F55.wireOp",EDGE,"E57"),sQuery(id+"F56.wireOp",EDGE,"E61")])]});
            var Q6;
            Q6=makeQuery(id+"F58.opSweep","SWEPT_BODY",BODY,{"disambiguationData":[OSD([sQuery(id+"F55.wireOp",EDGE,"E59"),sQuery(id+"F56.wireOp",EDGE,"E63")])]});
            var Q7;
            Q7=makeQuery(id+"F62.opExtrude","SWEPT_BODY",BODY,{"disambiguationData":[OSD([sQuery(id+"F61.wireOp",EDGE,"E75.bottom"),sQuery(id+"F61.wireOp",EDGE,"E75.top"),sQuery(id+"F61.wireOp",EDGE,"E75.left"),sQuery(id+"F61.wireOp",EDGE,"E75.right")])]});
            var Q8;
            Q8=makeQuery(id+"F63.opExtrude","SWEPT_BODY",BODY,{"disambiguationData":[OSD([sQuery(id+"F61.wireOp",EDGE,"E66.bottom"),sQuery(id+"F61.wireOp",EDGE,"E66.top"),sQuery(id+"F61.wireOp",EDGE,"E66.left"),sQuery(id+"F61.wireOp",EDGE,"E66.right")])]});
            var Q9;
            Q9=makeQuery(id+"F63.opExtrude","SWEPT_BODY",BODY,{"disambiguationData":[OSD([sQuery(id+"F61.wireOp",EDGE,"E67.bottom"),sQuery(id+"F61.wireOp",EDGE,"E67.top"),sQuery(id+"F61.wireOp",EDGE,"E67.left"),sQuery(id+"F61.wireOp",EDGE,"E67.right")])]});
            var Q10;
            Q10=makeQuery(id+"F63.opExtrude","SWEPT_BODY",BODY,{"disambiguationData":[OSD([sQuery(id+"F61.wireOp",EDGE,"E68.bottom"),sQuery(id+"F61.wireOp",EDGE,"E68.top"),sQuery(id+"F61.wireOp",EDGE,"E68.left"),sQuery(id+"F61.wireOp",EDGE,"E68.right")])]});
            var Q11;
            Q11=makeQuery(id+"F63.opExtrude","SWEPT_BODY",BODY,{"disambiguationData":[OSD([sQuery(id+"F61.wireOp",EDGE,"E73.bottom"),sQuery(id+"F61.wireOp",EDGE,"E73.top"),sQuery(id+"F61.wireOp",EDGE,"E73.left"),sQuery(id+"F61.wireOp",EDGE,"E73.right")])]});
            var Q12;
            Q12=makeQuery(id+"F63.opExtrude","SWEPT_BODY",BODY,{"disambiguationData":[OSD([sQuery(id+"F61.wireOp",EDGE,"E74.bottom"),sQuery(id+"F61.wireOp",EDGE,"E74.top"),sQuery(id+"F61.wireOp",EDGE,"E74.left"),sQuery(id+"F61.wireOp",EDGE,"E74.right")])]});
            var Q13;
            Q13=makeQuery(id+"F40.opExtrude","SWEPT_BODY",BODY,{"disambiguationData":[OSD([sQuery(id+"F35.wireOp",EDGE,"E30.bottom"),sQuery(id+"F35.wireOp",EDGE,"E30.top"),sQuery(id+"F35.wireOp",EDGE,"E30.left"),sQuery(id+"F35.wireOp",EDGE,"E30.right")])]});
            var Q14;
            Q14=makeQuery(id+"F39.opExtrude","SWEPT_BODY",BODY,{"disambiguationData":[OSD([sQuery(id+"F36.wireOp",EDGE,"E31.bottom"),sQuery(id+"F36.wireOp",EDGE,"E31.top"),sQuery(id+"F36.wireOp",EDGE,"E31.left"),sQuery(id+"F36.wireOp",EDGE,"E31.right")])]});
            var Q15;
            Q15=makeQuery(id+"F38.opExtrude","SWEPT_BODY",BODY,{"disambiguationData":[OSD([sQuery(id+"F37.wireOp",EDGE,"E32.bottom"),sQuery(id+"F37.wireOp",EDGE,"E32.top"),sQuery(id+"F37.wireOp",EDGE,"E32.left"),sQuery(id+"F37.wireOp",EDGE,"E32.right")])]});
            var Q16;
            Q16=makeQuery(id+"F32.opExtrude","SWEPT_BODY",BODY,{"disambiguationData":[OSD([sQuery(id+"F31.wireOp",EDGE,"E28")])]});
            var Q17;
            Q17=makeQuery(id+"F29.opExtrude","SWEPT_BODY",BODY,{"disambiguationData":[OSD([sQuery(id+"F28.wireOp",EDGE,"E27")])]});
            var Q18;
            Q18=makeQuery(id+"F22.opExtrude","SWEPT_BODY",BODY,{"disambiguationData":[OSD([sQuery(id+"F21.wireOp",EDGE,"E21")])]});
            var Q19;
            Q19=makeQuery(id+"F13.opSweep","SWEPT_BODY",BODY,{"disambiguationData":[OSD([sQuery(id+"F5.wireOp",EDGE,"E10"),sQuery(id+"F12.wireOp",EDGE,"E14")])]});
            var Q20;
            Q20=makeQuery(id+"F25.opExtrude","SWEPT_BODY",BODY,{"disambiguationData":[OSD([sQuery(id+"F24.wireOp",EDGE,"E23")])]});
            var Q21;
            Q21=sQuery(id+"F26.wireOp",VERTEX,"E25.end");
            transform(context, id + "F64", {"entities" : qUnion([Q0, Q1, Q2, Q3, Q4, Q5, Q6, Q7, Q8, Q9, Q10, Q11, Q12, Q13, Q14, Q15, Q16, Q17, Q18, Q19, Q20]), "transformType" : TransformType.SCALE_UNIFORMLY, "scale" : 1.25, "scalePoint" : qUnion([Q21]), "makeCopy" : false});
        }
    });
